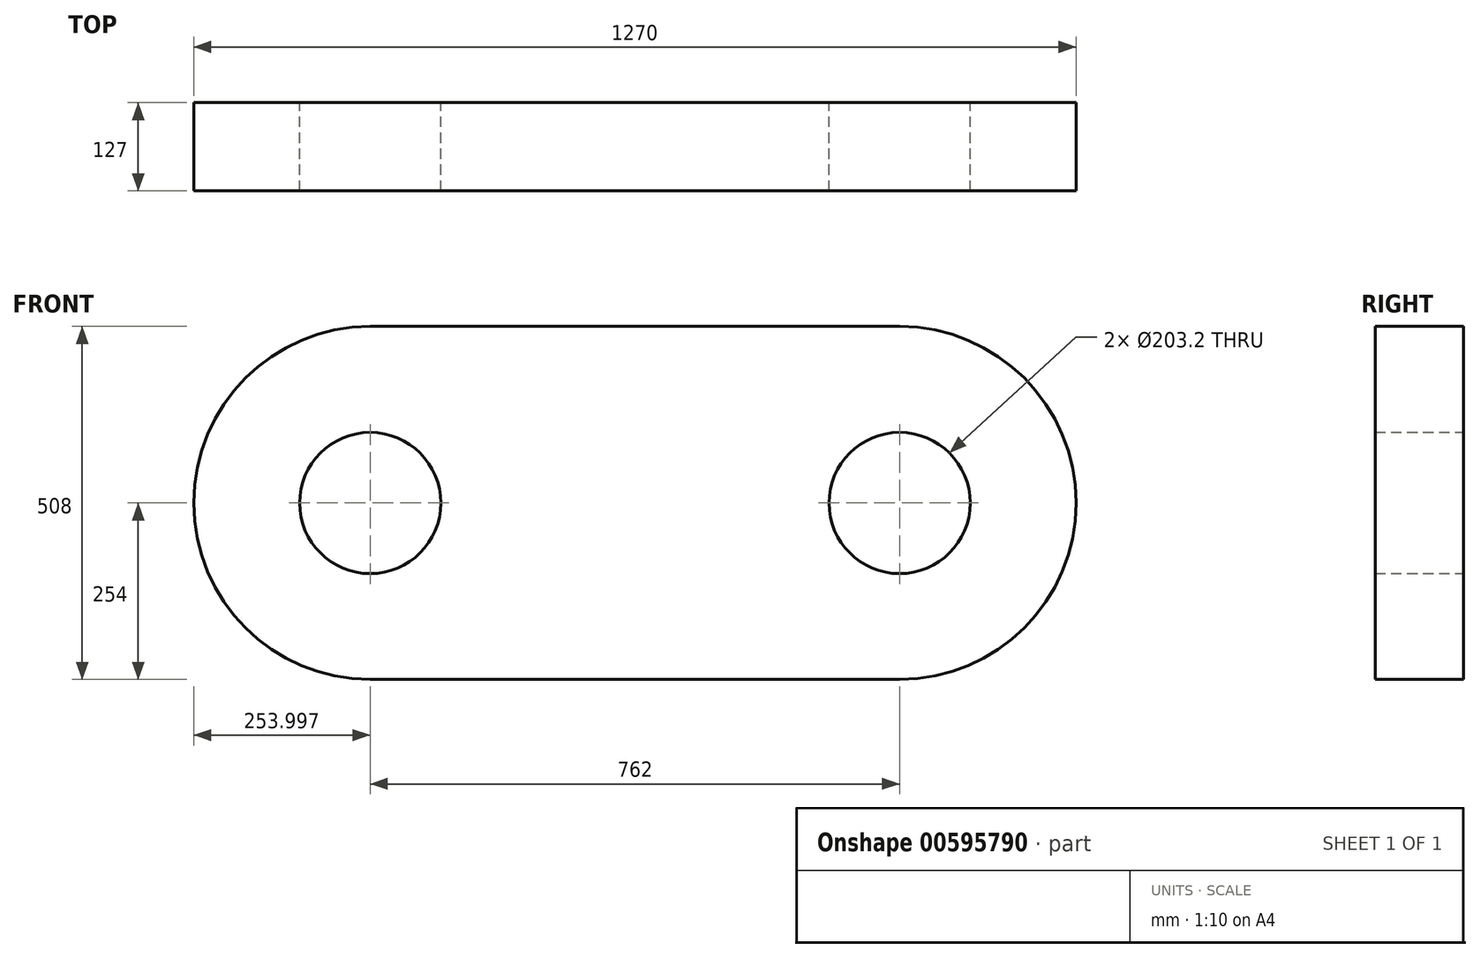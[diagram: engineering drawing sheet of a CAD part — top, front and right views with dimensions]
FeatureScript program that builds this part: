
annotation { "Feature Type Name" : "Feature", "Feature Type Description" : "" }
export const myFeature = defineFeature(function(context is Context, id is Id, definition is map)
    precondition{}
    {
        {
            var Q0;
            Q0=qCreatedBy(makeId("Front.planeOp"),FACE);
            var sketch = newSketch(context, id + "F0", { "sketchPlane" : qUnion([Q0])});
            skLineSegment(sketch, "E0.bottom", {"start": v(-38.03, 491.7) * mm, "end": v(723.97, 491.7) * mm});
            skLineSegment(sketch, "E0.top", {"start": v(-38.03, -16.3) * mm, "end": v(723.97, -16.3) * mm});
            skLineSegment(sketch, "E0.left", {"start": v(-38.03, 491.7) * mm, "end": v(-38.03, -16.3) * mm, "construction": true});
            skLineSegment(sketch, "E0.right", {"start": v(723.97, 491.7) * mm, "end": v(723.97, -16.3) * mm, "construction": true});
            skArc(sketch, "E1", {"start": v(-38.03, 491.7) * mm, "mid": v(-292.03, 237.7) * mm, "end": v(-38.03, -16.3) * mm});
            skArc(sketch, "E2", {"start": v(723.97, -16.3) * mm, "mid": v(977.97, 237.7) * mm, "end": v(723.97, 491.7) * mm});
            skCircle(sketch, "E3", {"center": v(-38.03, 237.7) * mm, "radius": 101.6 * mm});
            skCircle(sketch, "E4", {"center": v(723.97, 237.7) * mm, "radius": 101.6 * mm});
            skSolve(sketch);
        }
        {
            var Q0;
            Q0=makeQuery(id+"F0.imprint","IMPRINT",FACE,{"disambiguationData":[TD([[makeQuery(id+"F0.imprint","IMPRINT",EDGE,{"derivedFrom":sQuery(id+"F0.wireOp",EDGE,"E0.bottom")}),-1.0]])]});
            extrude(context, id + "F1", {"entities" : qUnion([Q0]), "depth" : 127 * mm, "offsetDistance" : 25.4 * mm});
        }
    });
